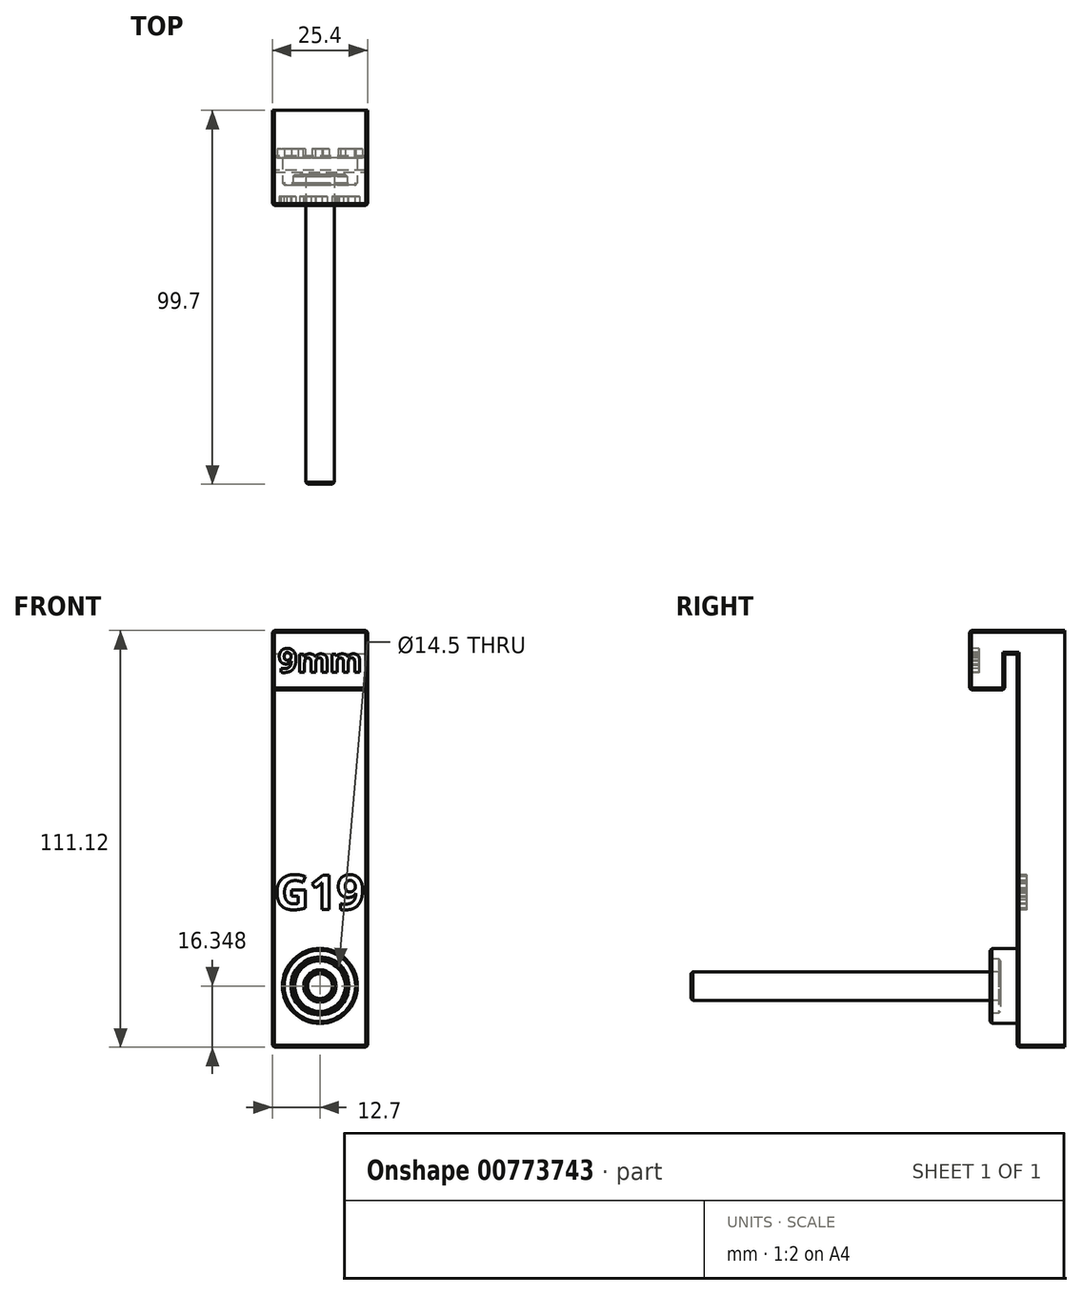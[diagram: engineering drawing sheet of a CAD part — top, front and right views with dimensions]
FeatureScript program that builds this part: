
annotation { "Feature Type Name" : "Feature", "Feature Type Description" : "" }
export const myFeature = defineFeature(function(context is Context, id is Id, definition is map)
    precondition{}
    {
        {
            var Q0;
            Q0=qCreatedBy(makeId("Right.planeOp"),FACE);
            var sketch = newSketch(context, id + "F0", { "sketchPlane" : qUnion([Q0])});
            skLineSegment(sketch, "E0.bottom", {"start": v(-12.7, 55.56) * mm, "end": v(12.7, 55.56) * mm});
            skLineSegment(sketch, "E0.top", {"start": v(-12.7, -55.56) * mm, "end": v(12.7, -55.56) * mm, "construction": true});
            skLineSegment(sketch, "E0.left", {"start": v(-12.7, 55.56) * mm, "end": v(-12.7, -55.56) * mm, "construction": true});
            skLineSegment(sketch, "E0.right", {"start": v(12.7, 55.56) * mm, "end": v(12.7, -55.56) * mm});
            skPoint(sketch, "E0.middle", {"position": v(0, 0) * mm});
            skLineSegment(sketch, "E1", {"start": v(-12.7, 55.56) * mm, "end": v(-12.7, 39.69) * mm});
            skLineSegment(sketch, "E2", {"start": v(-12.7, 39.69) * mm, "end": v(-3.3, 39.69) * mm});
            skLineSegment(sketch, "E3", {"start": v(-3.3, 39.69) * mm, "end": v(-3.3, 49.21) * mm});
            skLineSegment(sketch, "E4", {"start": v(-3.3, 49.21) * mm, "end": v(0, 49.21) * mm});
            skLineSegment(sketch, "E5", {"start": v(0, 49.21) * mm, "end": v(0, -55.56) * mm});
            skLineSegment(sketch, "E6", {"start": v(0, -55.56) * mm, "end": v(12.7, -55.56) * mm});
            skSolve(sketch);
        }
        {
            var Q0;
            Q0=qSketchRegion(id+"F0",true);
            extrude(context, id + "F1", {"entities" : qUnion([Q0]), "endBound" : BoundingType.SYMMETRIC, "depth" : 25.4 * mm, "offsetDistance" : 25.4 * mm});
        }
        {
            var Q0;
            Q0=qCreatedBy(makeId("Right.planeOp"),FACE);
            var sketch = newSketch(context, id + "F2", { "sketchPlane" : qUnion([Q0])});
            skLineSegment(sketch, "E7", {"start": v(0, -39.21) * mm, "end": v(-87, -39.21) * mm});
            skLineSegment(sketch, "E8", {"start": v(-87, -39.21) * mm, "end": v(87, -39.21) * mm, "construction": true});
            skLineSegment(sketch, "E9", {"start": v(0, -39.21) * mm, "end": v(0, -31.96) * mm});
            skLineSegment(sketch, "E10", {"start": v(0, -31.96) * mm, "end": v(-4.44, -31.96) * mm, "construction": true});
            skLineSegment(sketch, "E11", {"start": v(-4.44, -31.96) * mm, "end": v(-4.44, -35.4) * mm});
            skLineSegment(sketch, "E12", {"start": v(-4.44, -35.4) * mm, "end": v(-87, -35.4) * mm});
            skLineSegment(sketch, "E13", {"start": v(-87, -35.4) * mm, "end": v(-87, -39.21) * mm});
            skLineSegment(sketch, "E14", {"start": v(-178.45, -150.65) * mm, "end": v(-178.45, -23.65) * mm, "construction": true});
            skLineSegment(sketch, "E15", {"start": v(-178.45, -23.65) * mm, "end": v(-4.44, -23.65) * mm, "construction": true});
            skLineSegment(sketch, "E16", {"start": v(-4.45, -23.65) * mm, "end": v(-4.45, -150.65) * mm, "construction": true});
            skLineSegment(sketch, "E17", {"start": v(-4.44, -150.65) * mm, "end": v(-178.45, -150.65) * mm, "construction": true});
            skLineSegment(sketch, "E18", {"start": v(-7.2, -29.21) * mm, "end": v(-7.2, -31.96) * mm});
            skLineSegment(sketch, "E19", {"start": v(-4.44, -31.96) * mm, "end": v(-7.2, -31.96) * mm});
            skLineSegment(sketch, "E20", {"start": v(-7.2, -29.21) * mm, "end": v(0, -29.21) * mm});
            skLineSegment(sketch, "E21", {"start": v(0, -29.21) * mm, "end": v(0, -31.96) * mm});
            skLineSegment(sketch, "E22.MirrorCS", {"start": v(-7.2, -49.21) * mm, "end": v(0, -49.21) * mm, "construction": true});
            skSolve(sketch);
        }
        {
            var Q0;
            Q0=qSketchRegion(id+"F2",true);
            var Q1;
            Q1=sQuery(id+"F2.wireOp",EDGE,"E8");
            revolve(context, id + "F3", {"operationType" : NewBodyOperationType.ADD, "surfaceOperationType" : NewSurfaceOperationType.NEW, "entities" : qUnion([Q0]), "axis" : qUnion([Q1]), "revolveType" : RevolveType.FULL});
        }
        {
            var Q0;
            Q0=makeQuery(id+"F1.opExtrude","CAP_EDGE",EDGE,{"disambiguationData":[OSD([sQuery(id+"F0.wireOp",EDGE,"E0.bottom")])],"isStart":true});
            var Q1;
            Q1=makeQuery(id+"F1.opExtrude","CAP_EDGE",EDGE,{"disambiguationData":[OSD([sQuery(id+"F0.wireOp",EDGE,"E5")])],"isStart":true});
            var Q2;
            Q2=makeQuery(id+"F1.opExtrude","CAP_EDGE",EDGE,{"disambiguationData":[OSD([sQuery(id+"F0.wireOp",EDGE,"E6")])],"isStart":true});
            var Q3;
            Q3=makeQuery(id+"F1.opExtrude","CAP_EDGE",EDGE,{"disambiguationData":[OSD([sQuery(id+"F0.wireOp",EDGE,"E4")])],"isStart":true});
            var Q4;
            Q4=makeQuery(id+"F1.opExtrude","CAP_EDGE",EDGE,{"disambiguationData":[OSD([sQuery(id+"F0.wireOp",EDGE,"E3")])],"isStart":true});
            var Q5;
            Q5=makeQuery(id+"F1.opExtrude","CAP_EDGE",EDGE,{"disambiguationData":[OSD([sQuery(id+"F0.wireOp",EDGE,"E1")])],"isStart":true});
            var Q6;
            Q6=makeQuery(id+"F1.opExtrude","CAP_EDGE",EDGE,{"disambiguationData":[OSD([sQuery(id+"F0.wireOp",EDGE,"E2")])],"isStart":true});
            var Q7;
            Q7=makeQuery(id+"F1.opExtrude","CAP_EDGE",EDGE,{"disambiguationData":[OSD([sQuery(id+"F0.wireOp",EDGE,"E6")])],"isStart":false});
            var Q8;
            Q8=makeQuery(id+"F1.opExtrude","CAP_EDGE",EDGE,{"disambiguationData":[OSD([sQuery(id+"F0.wireOp",EDGE,"E0.bottom")])],"isStart":false});
            var Q9;
            Q9=makeQuery(id+"F1.opExtrude","CAP_EDGE",EDGE,{"disambiguationData":[OSD([sQuery(id+"F0.wireOp",EDGE,"E1")])],"isStart":false});
            var Q10;
            Q10=makeQuery(id+"F1.opExtrude","CAP_EDGE",EDGE,{"disambiguationData":[OSD([sQuery(id+"F0.wireOp",EDGE,"E4")])],"isStart":false});
            var Q11;
            Q11=makeQuery(id+"F1.opExtrude","CAP_EDGE",EDGE,{"disambiguationData":[OSD([sQuery(id+"F0.wireOp",EDGE,"E3")])],"isStart":false});
            var Q12;
            Q12=makeQuery(id+"F1.opExtrude","CAP_EDGE",EDGE,{"disambiguationData":[OSD([sQuery(id+"F0.wireOp",EDGE,"E2")])],"isStart":false});
            var Q13;
            Q13=makeQuery(id+"F1.opExtrude","CAP_EDGE",EDGE,{"disambiguationData":[OSD([sQuery(id+"F0.wireOp",EDGE,"E5")])],"isStart":false});
            var Q14;
            Q14=makeQuery(id+"F1.opExtrude","SWEPT_EDGE",EDGE,{"disambiguationData":[OSD([sQuery(id+"F0.wireOp",EDGE,"E5"),sQuery(id+"F0.wireOp",EDGE,"E6")])]});
            var Q15;
            Q15=makeQuery(id+"F1.opExtrude","SWEPT_FACE",FACE,{"disambiguationData":[OSD([sQuery(id+"F0.wireOp",EDGE,"E1")])]});
            var Q16;
            Q16=makeQuery(id+"F1.opExtrude","SWEPT_EDGE",EDGE,{"disambiguationData":[OSD([sQuery(id+"F0.wireOp",EDGE,"E2"),sQuery(id+"F0.wireOp",EDGE,"E3")])]});
            var Q17;
            Q17=makeQuery(id+"F3.opRevolve","SWEPT_EDGE",EDGE,{"disambiguationData":[OSD([sQuery(id+"F2.wireOp",EDGE,"E12"),sQuery(id+"F2.wireOp",EDGE,"E13")])]});
            var Q18;
            Q18=makeQuery(id+"F3.opRevolve","SWEPT_EDGE",EDGE,{"disambiguationData":[OSD([sQuery(id+"F2.wireOp",EDGE,"E10"),sQuery(id+"F2.wireOp",EDGE,"E11")])]});
            chamfer(context, id + "F4", {"entities" : qUnion([Q0, Q1, Q2, Q3, Q4, Q5, Q6, Q7, Q8, Q9, Q10, Q11, Q12, Q13, Q14, Q15, Q16, Q17, Q18]), "width" : .5 * mm, "tangentPropagation" : true});
        }
        {
            var Q0;
            Q0=makeQuery(id+"F1.opExtrude","SWEPT_FACE",FACE,{"disambiguationData":[OSD([sQuery(id+"F0.wireOp",EDGE,"E1")])]});
            var sketch = newSketch(context, id + "F5", { "sketchPlane" : qUnion([Q0])});
            skText(sketch, "E23", { "text": "9mm", "fontName": "OpenSans-Bold.ttf"});
            skLineSegment(sketch, "E24", {"start": v(0, 55.06) * mm, "end": v(0, 40.19) * mm, "construction": true});
            skLineSegment(sketch, "E25", {"start": v(-12.2, 47.62) * mm, "end": v(12.2, 47.62) * mm, "construction": true});
            skLineSegment(sketch, "E26", {"start": v(-11.13, 47.62) * mm, "end": v(11.13, 47.62) * mm, "construction": true});
            const initialGuessF5  = {"E23": [-0.01113, 0.04445, 1, 0, 0.00635]};
            skSetInitialGuess(sketch, initialGuessF5);
            skSolve(sketch);
        }
        {
            var Q0;
            Q0 = qSketchRegion(id + "F5", true);
            extrude(context, id + "F6", {"entities" : qUnion([Q0]), "operationType" : NewBodyOperationType.REMOVE, "oppositeDirection" : true, "depth" : 2.5 * mm, "offsetDistance" : 25.4 * mm});
        }
        {
            var Q0;
            Q0=makeQuery(id+"F3.opRevolve","SWEPT_EDGE",EDGE,{"disambiguationData":[OSD([sQuery(id+"F2.wireOp",EDGE,"E18"),sQuery(id+"F2.wireOp",EDGE,"E19")])]});
            var Q1;
            Q1=makeQuery(id+"F3.opRevolve","SWEPT_EDGE",EDGE,{"disambiguationData":[OSD([sQuery(id+"F2.wireOp",EDGE,"E18"),sQuery(id+"F2.wireOp",EDGE,"E20")])]});
            chamfer(context, id + "F7", {"entities" : qUnion([Q0, Q1]), "width" : .5 * mm, "tangentPropagation" : true});
        }
        {
            var Q0;
            Q0=makeQuery(id+"F1.opExtrude","SWEPT_FACE",FACE,{"disambiguationData":[OSD([sQuery(id+"F0.wireOp",EDGE,"E5")])]});
            var sketch = newSketch(context, id + "F8", { "sketchPlane" : qUnion([Q0])});
            skText(sketch, "E27", { "text": "G19", "fontName": "OpenSans-Bold.ttf"});
            skLineSegment(sketch, "E28", {"start": v(-12.2, 0) * mm, "end": v(12.2, 0) * mm, "construction": true});
            const initialGuessF8  = {"E27": [-0.0122, -0.0188, 1, 0, 0.00927]};
            skSetInitialGuess(sketch, initialGuessF8);
            skSolve(sketch);
        }
        {
            var Q0;
            Q0 = qSketchRegion(id + "F8", true);
            extrude(context, id + "F9", {"entities" : qUnion([Q0]), "operationType" : NewBodyOperationType.REMOVE, "oppositeDirection" : true, "depth" : 2.5 * mm, "offsetDistance" : 25.4 * mm});
        }
    });
